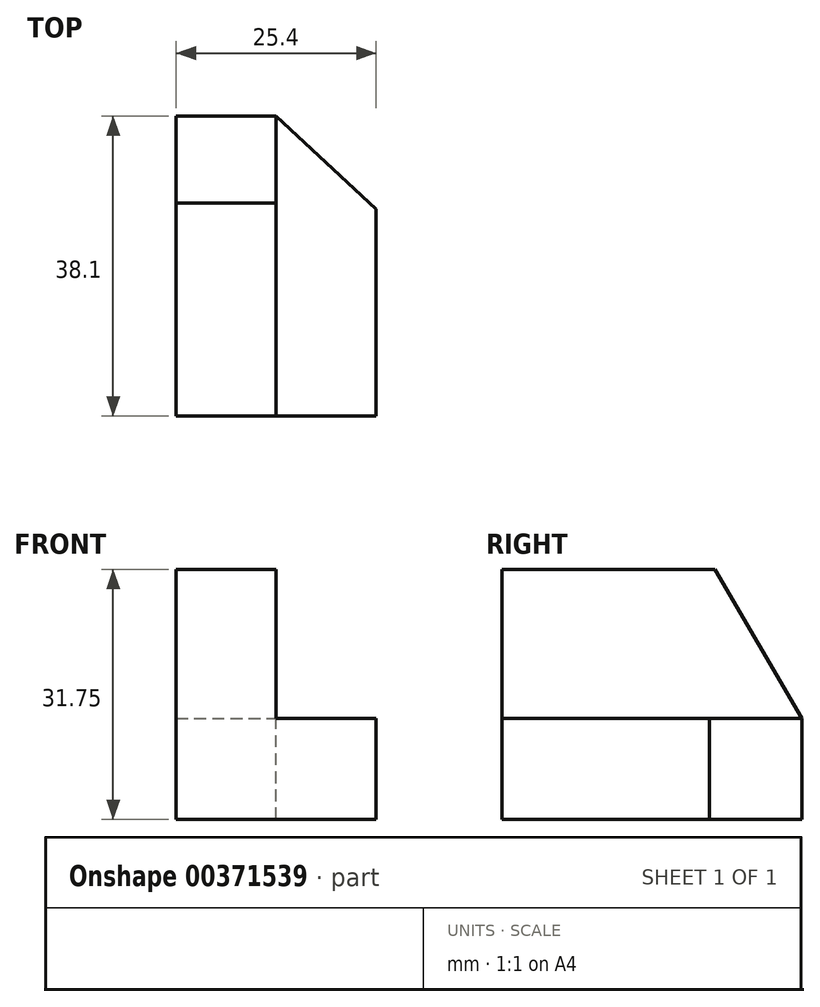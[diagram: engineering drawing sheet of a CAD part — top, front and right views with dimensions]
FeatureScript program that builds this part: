
annotation { "Feature Type Name" : "Feature", "Feature Type Description" : "" }
export const myFeature = defineFeature(function(context is Context, id is Id, definition is map)
    precondition{}
    {
        {
            var Q0;
            Q0=qCreatedBy(makeId("Right.planeOp"),FACE);
            var sketch = newSketch(context, id + "F0", { "sketchPlane" : qUnion([Q0])});
            skLineSegment(sketch, "E0", {"start": v(0, 0) * mm, "end": v(38.1, 0) * mm});
            skLineSegment(sketch, "E1", {"start": v(38.1, 0) * mm, "end": v(38.1, 31.75) * mm});
            skLineSegment(sketch, "E2", {"start": v(38.1, 31.75) * mm, "end": v(0, 31.75) * mm});
            skLineSegment(sketch, "E3", {"start": v(0, 31.75) * mm, "end": v(0, 0) * mm});
            skSolve(sketch);
        }
        {
            var Q0;
            Q0=makeQuery(id+"F0.imprint","IMPRINT",FACE,{"disambiguationData":[TD([[makeQuery(id+"F0.imprint","IMPRINT",EDGE,{"derivedFrom":sQuery(id+"F0.wireOp",EDGE,"E0")}),1.0]])]});
            extrude(context, id + "F1", {"entities" : qUnion([Q0]), "depth" : 25.4 * mm});
        }
        {
            var Q0;
            Q0=makeQuery(id+"F1.opExtrude","SWEPT_FACE",FACE,{"disambiguationData":[OSD([sQuery(id+"F0.wireOp",EDGE,"E2")])]});
            var sketch = newSketch(context, id + "F2", { "sketchPlane" : qUnion([Q0])});
            skLineSegment(sketch, "E4", {"start": v(12.7, 0) * mm, "end": v(12.7, 38.1) * mm});
            skSolve(sketch);
        }
        {
            var Q0;
            Q0 = qSketchRegion(id + "F2", true);
            var Q1;
            {var subQ0=sQuery(id+"F2.wireOp",EDGE,"E4");Q1=makeQuery(id+"F2.imprint","IMPRINT",FACE,{"disambiguationData":[TD([[makeQuery(id+"F2.imprint","IMPRINT",EDGE,{"derivedFrom":subQ0}),-1.0]])]});}
            extrude(context, id + "F3", {"entities" : qUnion([Q0, Q1]), "operationType" : NewBodyOperationType.REMOVE, "oppositeDirection" : true, "depth" : 25.4 * mm});
        }
        {
            var Q0;
            Q0=makeQuery(id+"F3.boolean.opBoolean","COPY",FACE,{"derivedFrom":makeQuery(id+"F3.opExtrude","SWEPT_FACE",FACE,{"disambiguationData":[OSD([sQuery(id+"F2.wireOp",EDGE,"E4")])]})});
            var sketch = newSketch(context, id + "F4", { "sketchPlane" : qUnion([Q0])});
            skLineSegment(sketch, "E5", {"start": v(0, 12.84) * mm, "end": v(38.1, 12.84) * mm});
            skSolve(sketch);
        }
        {
            var Q0;
            Q0 = qSketchRegion(id + "F4", true);
            var Q1;
            {var subQ0=sQuery(id+"F4.wireOp",EDGE,"E5");Q1=makeQuery(id+"F4.imprint","IMPRINT",FACE,{"disambiguationData":[TD([[makeQuery(id+"F4.imprint","IMPRINT",EDGE,{"derivedFrom":subQ0}),-1.0]])]});}
            extrude(context, id + "F5", {"entities" : qUnion([Q0, Q1]), "operationType" : NewBodyOperationType.ADD, "depth" : 12.7 * mm});
        }
        {
            var Q0;
            Q0=makeQuery(id+"F3.boolean.opBoolean","COPY",FACE,{"derivedFrom":makeQuery(id+"F3.opExtrude","SWEPT_FACE",FACE,{"disambiguationData":[OSD([sQuery(id+"F2.wireOp",EDGE,"E4")])]})});
            var sketch = newSketch(context, id + "F6", { "sketchPlane" : qUnion([Q0])});
            skLineSegment(sketch, "E6", {"start": v(38.1, 12.84) * mm, "end": v(27.02, 31.75) * mm});
            skSolve(sketch);
        }
        {
            var Q0;
            Q0 = qSketchRegion(id + "F6", true);
            var Q1;
            {var subQ0=sQuery(id+"F6.wireOp",EDGE,"E6");Q1=makeQuery(id+"F6.imprint","IMPRINT",FACE,{"disambiguationData":[TD([[makeQuery(id+"F6.imprint","IMPRINT",EDGE,{"derivedFrom":subQ0}),-1.0]])]});}
            extrude(context, id + "F7", {"entities" : qUnion([Q0, Q1]), "operationType" : NewBodyOperationType.REMOVE, "oppositeDirection" : true, "depth" : 25.4 * mm});
        }
        {
            var Q0;
            Q0=makeQuery(id+"F5.opExtrude","SWEPT_FACE",FACE,{"disambiguationData":[OSD([sQuery(id+"F4.wireOp",EDGE,"E5")])]});
            var sketch = newSketch(context, id + "F8", { "sketchPlane" : qUnion([Q0])});
            skLineSegment(sketch, "E7", {"start": v(12.7, 38.1) * mm, "end": v(25.4, 26.3) * mm});
            skSolve(sketch);
        }
        {
            var Q0;
            Q0 = qSketchRegion(id + "F8", true);
            var Q1;
            {var subQ0=sQuery(id+"F8.wireOp",EDGE,"E7");Q1=makeQuery(id+"F8.imprint","IMPRINT",FACE,{"disambiguationData":[TD([[makeQuery(id+"F8.imprint","IMPRINT",EDGE,{"derivedFrom":subQ0}),1.0]])]});}
            extrude(context, id + "F9", {"entities" : qUnion([Q0, Q1]), "operationType" : NewBodyOperationType.REMOVE, "oppositeDirection" : true, "depth" : 25.4 * mm});
        }
    });
